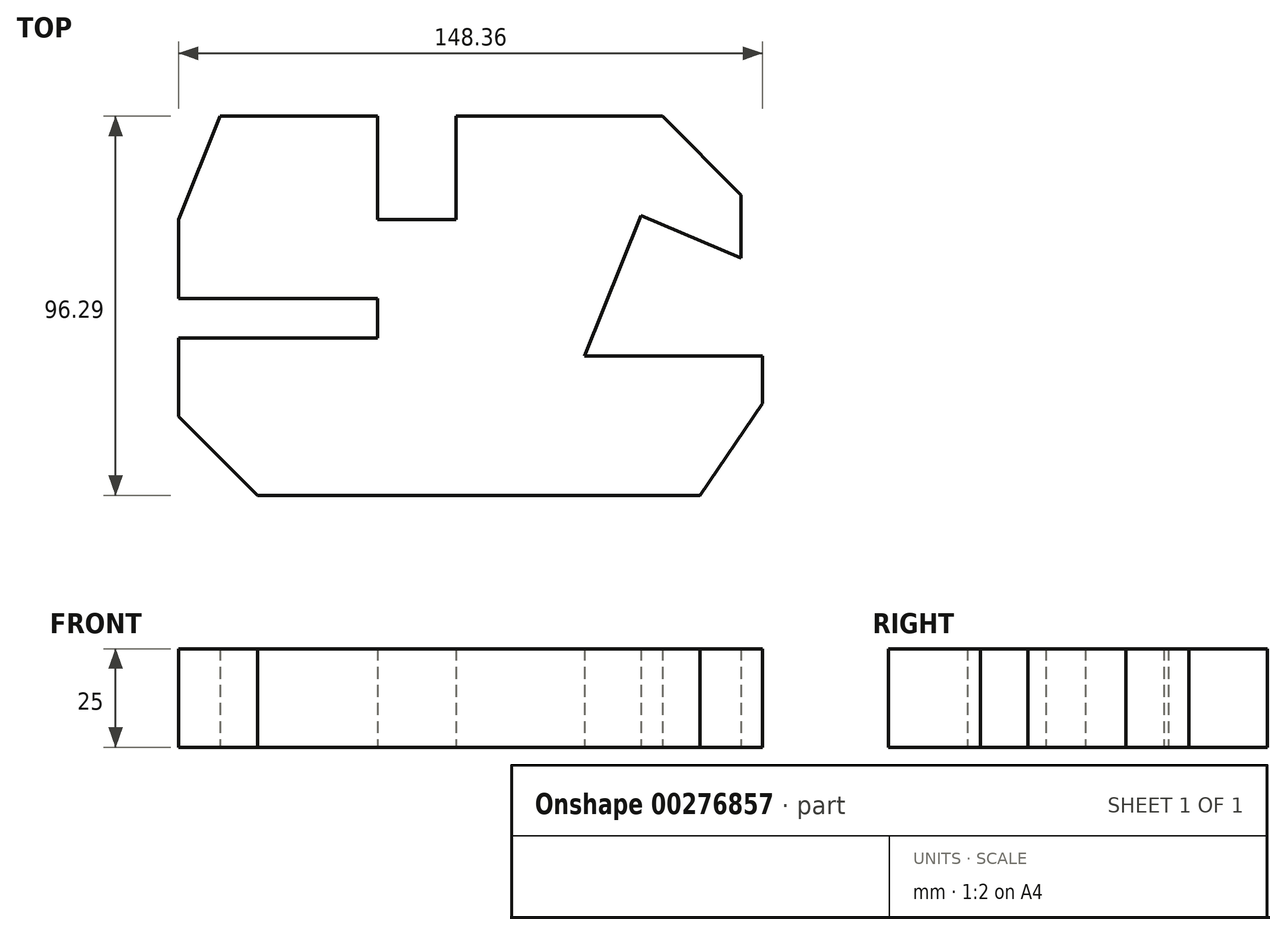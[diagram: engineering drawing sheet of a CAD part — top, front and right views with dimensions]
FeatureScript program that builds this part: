
annotation { "Feature Type Name" : "Feature", "Feature Type Description" : "" }
export const myFeature = defineFeature(function(context is Context, id is Id, definition is map)
    precondition{}
    {
        {
            var Q0;
            Q0=qCreatedBy(makeId("Top.planeOp"),FACE);
            var sketch = newSketch(context, id + "F0", { "sketchPlane" : qUnion([Q0])});
            skLineSegment(sketch, "E0", {"start": v(-60, 60.91) * mm, "end": v(-20, 60.91) * mm});
            skLineSegment(sketch, "E1", {"start": v(-20, 34.63) * mm, "end": v(-20, 60.91) * mm});
            skLineSegment(sketch, "E2", {"start": v(-20, 34.63) * mm, "end": v(0, 34.63) * mm});
            skLineSegment(sketch, "E3", {"start": v(0, 60.91) * mm, "end": v(0, 34.63) * mm});
            skLineSegment(sketch, "E4", {"start": v(0, 60.91) * mm, "end": v(52.4, 60.91) * mm});
            skLineSegment(sketch, "E5", {"start": v(52.4, 60.91) * mm, "end": v(72.41, 40.9) * mm});
            skLineSegment(sketch, "E6", {"start": v(72.41, 40.9) * mm, "end": v(72.41, 24.9) * mm});
            skLineSegment(sketch, "E7", {"start": v(72.41, 24.9) * mm, "end": v(46.98, 35.7) * mm});
            skLineSegment(sketch, "E8", {"start": v(46.98, 35.7) * mm, "end": v(32.56, 0) * mm});
            skLineSegment(sketch, "E9", {"start": v(32.56, 0) * mm, "end": v(77.86, 0) * mm});
            skLineSegment(sketch, "E10", {"start": v(77.86, 0) * mm, "end": v(77.86, -12) * mm});
            skLineSegment(sketch, "E11", {"start": v(77.86, -12) * mm, "end": v(61.91, -35.38) * mm});
            skLineSegment(sketch, "E12", {"start": v(61.91, -35.38) * mm, "end": v(-50.49, -35.38) * mm});
            skLineSegment(sketch, "E13", {"start": v(-50.49, -35.38) * mm, "end": v(-70.5, -15.37) * mm});
            skLineSegment(sketch, "E14", {"start": v(-70.5, -15.37) * mm, "end": v(-70.5, 4.63) * mm});
            skLineSegment(sketch, "E15", {"start": v(-70.5, 4.63) * mm, "end": v(-20, 4.63) * mm});
            skLineSegment(sketch, "E16", {"start": v(-20, 4.63) * mm, "end": v(-20, 14.63) * mm});
            skLineSegment(sketch, "E17", {"start": v(-20, 14.63) * mm, "end": v(-70.5, 14.63) * mm});
            skLineSegment(sketch, "E18", {"start": v(-70.5, 14.63) * mm, "end": v(-70.5, 34.63) * mm});
            skLineSegment(sketch, "E19", {"start": v(-70.5, 34.63) * mm, "end": v(-60, 60.91) * mm});
            skSolve(sketch);
        }
        {
            var Q0;
            Q0=makeQuery(id+"F0.imprint","IMPRINT",FACE,{"disambiguationData":[TD([[makeQuery(id+"F0.imprint","IMPRINT",EDGE,{"derivedFrom":sQuery(id+"F0.wireOp",EDGE,"E0")}),-1.0]])]});
            extrude(context, id + "F1", {"entities" : qUnion([Q0]), "depth" : 25 * mm});
        }
    });
